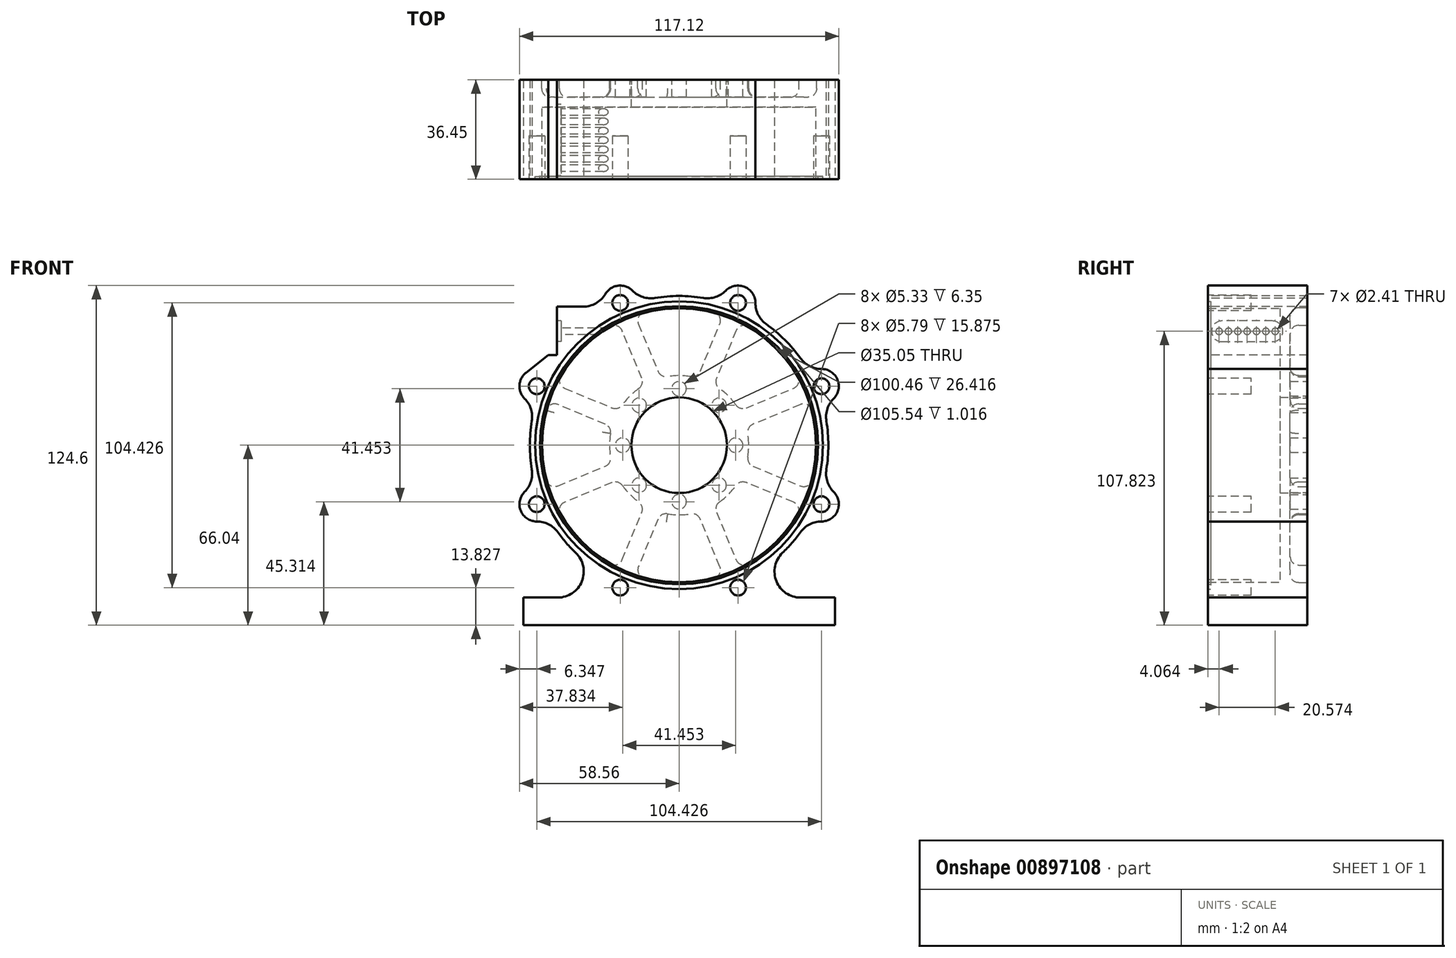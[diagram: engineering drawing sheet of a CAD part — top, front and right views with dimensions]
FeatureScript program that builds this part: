
annotation { "Feature Type Name" : "Feature", "Feature Type Description" : "" }
export const myFeature = defineFeature(function(context is Context, id is Id, definition is map)
    precondition{}
    {
        {
            var Q0;
            Q0=qCreatedBy(makeId("Front.planeOp"),FACE);
            var sketch = newSketch(context, id + "F0", { "sketchPlane" : qUnion([Q0])});
            skCircle(sketch, "E0", {"center": v(0, 0) * mm, "radius": 50.17 * mm, "construction": true});
            skArc(sketch, "E1", {"start": v(54.02, -8.84) * mm, "mid": v(54.74, 0) * mm, "end": v(54.02, 8.84) * mm});
            skCircle(sketch, "E2.cCircle", {"center": v(0, 0) * mm, "radius": 56.52 * mm, "construction": true});
            skLineSegment(sketch, "E2.0", {"start": v(52.21, -21.63) * mm, "end": v(21.63, -52.21) * mm, "construction": true});
            skLineSegment(sketch, "E2.1", {"start": v(21.63, -52.21) * mm, "end": v(-21.63, -52.21) * mm, "construction": true});
            skLineSegment(sketch, "E2.2", {"start": v(-21.63, -52.21) * mm, "end": v(-52.21, -21.63) * mm, "construction": true});
            skLineSegment(sketch, "E2.3", {"start": v(-52.21, -21.63) * mm, "end": v(-52.21, 21.63) * mm, "construction": true});
            skLineSegment(sketch, "E2.4", {"start": v(-52.21, 21.63) * mm, "end": v(-21.63, 52.21) * mm, "construction": true});
            skLineSegment(sketch, "E2.5", {"start": v(-21.63, 52.21) * mm, "end": v(21.63, 52.21) * mm, "construction": true});
            skLineSegment(sketch, "E2.6", {"start": v(21.63, 52.21) * mm, "end": v(52.21, 21.63) * mm, "construction": true});
            skLineSegment(sketch, "E2.7", {"start": v(52.21, 21.63) * mm, "end": v(52.21, -21.63) * mm, "construction": true});
            skArc(sketch, "E3", {"start": v(27.98, 52.2) * mm, "mid": v(24.06, 58.08) * mm, "end": v(17.13, 56.7) * mm});
            skArc(sketch, "E4", {"start": v(56.7, 17.13) * mm, "mid": v(58.08, 24.06) * mm, "end": v(52.2, 27.98) * mm});
            skArc(sketch, "E5", {"start": v(52.2, -27.98) * mm, "mid": v(58.08, -24.06) * mm, "end": v(56.7, -17.13) * mm});
            skArc(sketch, "E6", {"start": v(-56.7, -17.13) * mm, "mid": v(-58.08, -24.06) * mm, "end": v(-52.2, -27.98) * mm});
            skArc(sketch, "E7", {"start": v(-56.13, 26.62) * mm, "mid": v(-58.55, 22) * mm, "end": v(-56.7, 17.13) * mm});
            skArc(sketch, "E8.trimOffspring", {"start": v(44.45, 31.94) * mm, "mid": v(38.7, 38.7) * mm, "end": v(31.94, 44.45) * mm});
            skArc(sketch, "E9.trimOffspring", {"start": v(8.84, 54.02) * mm, "mid": v(0, 54.74) * mm, "end": v(-8.84, 54.02) * mm});
            skArc(sketch, "E10.trimOffspring", {"start": v(-54.02, 8.84) * mm, "mid": v(-54.74, 0) * mm, "end": v(-54.02, -8.84) * mm});
            skArc(sketch, "E11.trimOffspring", {"start": v(-44.45, -31.94) * mm, "mid": v(-41.35, -35.86) * mm, "end": v(-37.9, -39.48) * mm});
            skArc(sketch, "E12.trimOffspring", {"start": v(37.9, -39.48) * mm, "mid": v(41.35, -35.86) * mm, "end": v(44.45, -31.94) * mm});
            skLineSegment(sketch, "E13", {"start": v(-57.15, -55.88) * mm, "end": v(-57.15, -66.04) * mm});
            skLineSegment(sketch, "E14", {"start": v(-57.15, -66.04) * mm, "end": v(57.15, -66.04) * mm});
            skLineSegment(sketch, "E15", {"start": v(57.15, -66.04) * mm, "end": v(57.15, -55.88) * mm});
            skLineSegment(sketch, "E16", {"start": v(57.15, -55.88) * mm, "end": v(44.5, -55.88) * mm});
            skLineSegment(sketch, "E17", {"start": v(-57.15, -55.88) * mm, "end": v(-44.5, -55.88) * mm});
            skPoint(sketch, "E18", {"position": v(0, -66.04) * mm});
            skArc(sketch, "E19", {"start": v(-44.5, -55.88) * mm, "mid": v(-35.67, -49.91) * mm, "end": v(-37.9, -39.48) * mm});
            skArc(sketch, "E20", {"start": v(37.9, -39.48) * mm, "mid": v(35.67, -49.91) * mm, "end": v(44.5, -55.88) * mm});
            skPoint(sketch, "E21.visualSharp", {"position": v(-47.97, -26.36) * mm});
            skArc(sketch, "E21.filletArc", {"start": v(-44.45, -31.94) * mm, "mid": v(-47.85, -29.02) * mm, "end": v(-52.2, -27.98) * mm});
            skPoint(sketch, "E22.visualSharp", {"position": v(-52.56, -15.29) * mm});
            skArc(sketch, "E22.filletArc", {"start": v(-56.7, -17.13) * mm, "mid": v(-54.35, -13.3) * mm, "end": v(-54.02, -8.84) * mm});
            skPoint(sketch, "E23.visualSharp", {"position": v(-52.56, 15.29) * mm});
            skArc(sketch, "E23.filletArc", {"start": v(-54.02, 8.84) * mm, "mid": v(-54.35, 13.3) * mm, "end": v(-56.7, 17.13) * mm});
            skPoint(sketch, "E24.visualSharp", {"position": v(47.97, -26.36) * mm});
            skArc(sketch, "E24.filletArc", {"start": v(52.2, -27.98) * mm, "mid": v(47.85, -29.02) * mm, "end": v(44.45, -31.94) * mm});
            skPoint(sketch, "E25.visualSharp", {"position": v(52.56, -15.29) * mm});
            skArc(sketch, "E25.filletArc", {"start": v(54.02, -8.84) * mm, "mid": v(54.35, -13.3) * mm, "end": v(56.7, -17.13) * mm});
            skPoint(sketch, "E26.visualSharp", {"position": v(52.56, 15.29) * mm});
            skArc(sketch, "E26.filletArc", {"start": v(56.7, 17.13) * mm, "mid": v(54.35, 13.3) * mm, "end": v(54.02, 8.84) * mm});
            skPoint(sketch, "E27.visualSharp", {"position": v(47.97, 26.36) * mm});
            skArc(sketch, "E27.filletArc", {"start": v(44.45, 31.94) * mm, "mid": v(47.85, 29.02) * mm, "end": v(52.2, 27.98) * mm});
            skPoint(sketch, "E28.visualSharp", {"position": v(26.36, 47.97) * mm});
            skArc(sketch, "E28.filletArc", {"start": v(27.98, 52.2) * mm, "mid": v(29.02, 47.85) * mm, "end": v(31.94, 44.45) * mm});
            skPoint(sketch, "E29.visualSharp", {"position": v(15.29, 52.56) * mm});
            skArc(sketch, "E29.filletArc", {"start": v(8.84, 54.02) * mm, "mid": v(13.3, 54.35) * mm, "end": v(17.13, 56.7) * mm});
            skPoint(sketch, "E30.visualSharp", {"position": v(-15.29, 52.56) * mm});
            skLineSegment(sketch, "E31", {"start": v(-35.27, 50.8) * mm, "end": v(-44.8, 50.8) * mm});
            skLineSegment(sketch, "E32", {"start": v(-44.8, 50.8) * mm, "end": v(-44.8, 33.02) * mm});
            skArc(sketch, "E33", {"start": v(-17.13, 56.7) * mm, "mid": v(-22.41, 58.51) * mm, "end": v(-27.09, 55.46) * mm});
            skArc(sketch, "E34.filletArc", {"start": v(-17.13, 56.7) * mm, "mid": v(-13.3, 54.35) * mm, "end": v(-8.84, 54.02) * mm});
            skPoint(sketch, "E35.visualSharp", {"position": v(-27.82, 50.8) * mm});
            skArc(sketch, "E35.filletArc", {"start": v(-35.27, 50.8) * mm, "mid": v(-30.56, 52.05) * mm, "end": v(-27.09, 55.46) * mm});
            skLineSegment(sketch, "E36", {"start": v(-44.8, 33.02) * mm, "end": v(-47.97, 33.02) * mm});
            skLineSegment(sketch, "E37", {"start": v(-47.97, 33.02) * mm, "end": v(-56.13, 26.62) * mm});
            skSolve(sketch);
        }
        {
            var Q0;
            Q0=qSketchRegion(id+"F0",true);
            extrude(context, id + "F1", {"entities" : qUnion([Q0]), "oppositeDirection" : true, "depth" : 36.45 * mm});
        }
        {
            var Q0;
            Q0=qCreatedBy(makeId("Right.planeOp"),FACE);
            var sketch = newSketch(context, id + "F2", { "sketchPlane" : qUnion([Q0])});
            skLineSegment(sketch, "E38", {"start": v(0, 0) * mm, "end": v(0, 50.23) * mm});
            skLineSegment(sketch, "E39", {"start": v(26.42, 50.23) * mm, "end": v(0, 50.23) * mm});
            skLineSegment(sketch, "E40", {"start": v(26.42, 50.23) * mm, "end": v(26.42, 17.53) * mm});
            skLineSegment(sketch, "E41", {"start": v(36.45, 17.53) * mm, "end": v(26.42, 17.53) * mm});
            skLineSegment(sketch, "E42", {"start": v(36.45, 17.53) * mm, "end": v(36.45, 0) * mm});
            skLineSegment(sketch, "E43", {"start": v(0, 0) * mm, "end": v(36.45, 0) * mm});
            skLineSegment(sketch, "E44.bottom", {"start": v(1.02, 51) * mm, "end": v(0, 51) * mm});
            skLineSegment(sketch, "E44.top", {"start": v(1.02, 52.77) * mm, "end": v(0, 52.77) * mm});
            skLineSegment(sketch, "E44.left", {"start": v(0, 51) * mm, "end": v(0, 52.77) * mm});
            skLineSegment(sketch, "E44.right", {"start": v(1.02, 51) * mm, "end": v(1.02, 52.77) * mm});
            skSolve(sketch);
        }
        {
            var Q0;
            Q0=qSketchRegion(id+"F2",true);
            var Q1;
            Q1=sQuery(id+"F2.wireOp",EDGE,"E43");
            revolve(context, id + "F3", {"operationType" : NewBodyOperationType.REMOVE, "entities" : qUnion([Q0]), "axis" : qUnion([Q1]), "revolveType" : RevolveType.FULL, "oppositeDirection" : true});
        }
        {
            var Q0;
            Q0=makeQuery(id+"F1.opExtrude","SWEPT_FACE",FACE,{"disambiguationData":[OSD([sQuery(id+"F0.wireOp",EDGE,"E32")])]});
            var sketch = newSketch(context, id + "F4", { "sketchPlane" : qUnion([Q0])});
            skLineSegment(sketch, "E45", {"start": v(-23.62, 45.6) * mm, "end": v(-5.08, 45.6) * mm});
            skLineSegment(sketch, "E46", {"start": v(-5.08, 37.97) * mm, "end": v(-23.62, 37.97) * mm});
            skArc(sketch, "E47", {"start": v(-23.62, 45.6) * mm, "mid": v(-27.43, 41.78) * mm, "end": v(-23.62, 37.97) * mm});
            skArc(sketch, "E48", {"start": v(-5.08, 37.97) * mm, "mid": v(-1.27, 41.78) * mm, "end": v(-5.08, 45.6) * mm});
            skSolve(sketch);
        }
        {
            var Q0;
            Q0=qSketchRegion(id+"F4",true);
            extrude(context, id + "F5", {"entities" : qUnion([Q0]), "operationType" : NewBodyOperationType.REMOVE, "oppositeDirection" : true, "depth" : 1.52 * mm});
        }
        {
            var Q0;
            Q0=makeQuery(id+"F5.boolean.opBoolean","COPY",FACE,{"derivedFrom":makeQuery(id+"F5.opExtrude","CAP_FACE",FACE,{"disambiguationData":[OSD([sQuery(id+"F4.wireOp",EDGE,"E45"),sQuery(id+"F4.wireOp",EDGE,"E46"),sQuery(id+"F4.wireOp",EDGE,"E47"),sQuery(id+"F4.wireOp",EDGE,"E48")])],"isStart":false})});
            var sketch = newSketch(context, id + "F6", { "sketchPlane" : qUnion([Q0])});
            skCircle(sketch, "E49", {"center": v(-4.06, 41.78) * mm, "radius": 1.2 * mm});
            skPoint(sketch, "E50", {"position": v(-1.27, 41.78) * mm});
            skCircle(sketch, "E51.1.0.0", {"center": v(-7.5, 41.78) * mm, "radius": 1.2 * mm});
            skCircle(sketch, "E51.2.0.0", {"center": v(-10.92, 41.78) * mm, "radius": 1.2 * mm});
            skCircle(sketch, "E51.3.0.0", {"center": v(-14.35, 41.78) * mm, "radius": 1.2 * mm});
            skCircle(sketch, "E51.4.0.0", {"center": v(-17.78, 41.78) * mm, "radius": 1.2 * mm});
            skCircle(sketch, "E51.5.0.0", {"center": v(-21.2, 41.78) * mm, "radius": 1.2 * mm});
            skCircle(sketch, "E51.6.0.0", {"center": v(-24.64, 41.78) * mm, "radius": 1.2 * mm});
            skLineSegment(sketch, "E51.direction1", {"start": v(-4.06, 41.78) * mm, "end": v(-7.5, 41.78) * mm, "construction": true});
            skSolve(sketch);
        }
        {
            var Q0;
            Q0=qSketchRegion(id+"F6",true);
            extrude(context, id + "F7", {"entities" : qUnion([Q0]), "operationType" : NewBodyOperationType.REMOVE, "oppositeDirection" : true, "depth" : 25.4 * mm});
        }
        {
            var Q0;
            Q0=makeQuery(id+"F1.opExtrude","CAP_FACE",FACE,{"disambiguationData":[OSD([sQuery(id+"F0.wireOp",EDGE,"E1"),sQuery(id+"F0.wireOp",EDGE,"E3"),sQuery(id+"F0.wireOp",EDGE,"E4"),sQuery(id+"F0.wireOp",EDGE,"E5"),sQuery(id+"F0.wireOp",EDGE,"E6"),sQuery(id+"F0.wireOp",EDGE,"E7"),sQuery(id+"F0.wireOp",EDGE,"E8.trimOffspring"),sQuery(id+"F0.wireOp",EDGE,"E9.trimOffspring"),sQuery(id+"F0.wireOp",EDGE,"E10.trimOffspring"),sQuery(id+"F0.wireOp",EDGE,"E11.trimOffspring"),sQuery(id+"F0.wireOp",EDGE,"E12.trimOffspring"),sQuery(id+"F0.wireOp",EDGE,"E13"),sQuery(id+"F0.wireOp",EDGE,"E14"),sQuery(id+"F0.wireOp",EDGE,"E15"),sQuery(id+"F0.wireOp",EDGE,"E16"),sQuery(id+"F0.wireOp",EDGE,"E17"),sQuery(id+"F0.wireOp",EDGE,"E19"),sQuery(id+"F0.wireOp",EDGE,"E20"),sQuery(id+"F0.wireOp",EDGE,"E21.filletArc"),sQuery(id+"F0.wireOp",EDGE,"E22.filletArc"),sQuery(id+"F0.wireOp",EDGE,"E23.filletArc"),sQuery(id+"F0.wireOp",EDGE,"E24.filletArc"),sQuery(id+"F0.wireOp",EDGE,"E25.filletArc"),sQuery(id+"F0.wireOp",EDGE,"E26.filletArc"),sQuery(id+"F0.wireOp",EDGE,"E27.filletArc"),sQuery(id+"F0.wireOp",EDGE,"E28.filletArc"),sQuery(id+"F0.wireOp",EDGE,"E29.filletArc"),sQuery(id+"F0.wireOp",EDGE,"E31"),sQuery(id+"F0.wireOp",EDGE,"E32"),sQuery(id+"F0.wireOp",EDGE,"E33"),sQuery(id+"F0.wireOp",EDGE,"E34.filletArc"),sQuery(id+"F0.wireOp",EDGE,"E35.filletArc"),sQuery(id+"F0.wireOp",EDGE,"E36"),sQuery(id+"F0.wireOp",EDGE,"E37")])],"isStart":false});
            var sketch = newSketch(context, id + "F8", { "sketchPlane" : qUnion([Q0])});
            skPoint(sketch, "E52.center", {"position": v(0, 0) * mm});
            skArc(sketch, "E53", {"start": v(4.25, 25.17) * mm, "mid": v(0, 25.53) * mm, "end": v(-4.25, 25.17) * mm});
            skLineSegment(sketch, "E54", {"start": v(0, 0) * mm, "end": v(24.06, 58.08) * mm, "construction": true});
            skLineSegment(sketch, "E55", {"start": v(0, 0) * mm, "end": v(0, 17.53) * mm, "construction": true});
            skArc(sketch, "E56", {"start": v(12.8, 48.77) * mm, "mid": v(0, 50.42) * mm, "end": v(-12.8, 48.77) * mm});
            skLineSegment(sketch, "E57", {"start": v(14.92, 44.48) * mm, "end": v(7.71, 27.09) * mm});
            skLineSegment(sketch, "E58", {"start": v(-7.71, 27.09) * mm, "end": v(-14.92, 44.48) * mm});
            skPoint(sketch, "E59.visualSharp", {"position": v(-16.26, 47.72) * mm});
            skArc(sketch, "E59.filletArc", {"start": v(-12.8, 48.77) * mm, "mid": v(-14.83, 47.1) * mm, "end": v(-14.92, 44.48) * mm});
            skPoint(sketch, "E60.visualSharp", {"position": v(16.26, 47.72) * mm});
            skArc(sketch, "E60.filletArc", {"start": v(14.92, 44.48) * mm, "mid": v(14.83, 47.1) * mm, "end": v(12.8, 48.77) * mm});
            skPoint(sketch, "E61.visualSharp", {"position": v(6.7, 24.63) * mm});
            skArc(sketch, "E61.filletArc", {"start": v(4.25, 25.17) * mm, "mid": v(6.32, 25.52) * mm, "end": v(7.71, 27.09) * mm});
            skPoint(sketch, "E62.visualSharp", {"position": v(-6.7, 24.63) * mm});
            skArc(sketch, "E62.filletArc", {"start": v(-7.71, 27.09) * mm, "mid": v(-6.32, 25.52) * mm, "end": v(-4.25, 25.17) * mm});
            skArc(sketch, "E63.1.0", {"start": v(-43.53, 25.44) * mm, "mid": v(-43.8, 22.82) * mm, "end": v(-42, 20.9) * mm});
            skLineSegment(sketch, "E63.1.1", {"start": v(-24.6, 13.7) * mm, "end": v(-42, 20.9) * mm});
            skArc(sketch, "E63.1.2", {"start": v(-14.8, 20.8) * mm, "mid": v(-18.05, 18.05) * mm, "end": v(-20.8, 14.8) * mm});
            skArc(sketch, "E63.1.3", {"start": v(-24.6, 13.7) * mm, "mid": v(-22.51, 13.58) * mm, "end": v(-20.8, 14.8) * mm});
            skArc(sketch, "E63.1.4", {"start": v(-14.8, 20.8) * mm, "mid": v(-13.58, 22.51) * mm, "end": v(-13.7, 24.6) * mm});
            skLineSegment(sketch, "E63.1.5", {"start": v(-20.9, 42) * mm, "end": v(-13.7, 24.6) * mm});
            skArc(sketch, "E63.1.6", {"start": v(-20.9, 42) * mm, "mid": v(-22.82, 43.8) * mm, "end": v(-25.44, 43.53) * mm});
            skArc(sketch, "E63.1.7", {"start": v(-25.44, 43.53) * mm, "mid": v(-35.65, 35.65) * mm, "end": v(-43.53, 25.44) * mm});
            skArc(sketch, "E63.2.0", {"start": v(-48.77, -12.8) * mm, "mid": v(-47.1, -14.83) * mm, "end": v(-44.48, -14.92) * mm});
            skLineSegment(sketch, "E63.2.1", {"start": v(-27.09, -7.71) * mm, "end": v(-44.48, -14.92) * mm});
            skArc(sketch, "E63.2.2", {"start": v(-25.17, 4.25) * mm, "mid": v(-25.53, 0) * mm, "end": v(-25.17, -4.25) * mm});
            skArc(sketch, "E63.2.3", {"start": v(-27.09, -7.71) * mm, "mid": v(-25.52, -6.32) * mm, "end": v(-25.17, -4.25) * mm});
            skArc(sketch, "E63.2.4", {"start": v(-25.17, 4.25) * mm, "mid": v(-25.52, 6.32) * mm, "end": v(-27.09, 7.71) * mm});
            skLineSegment(sketch, "E63.2.5", {"start": v(-44.48, 14.92) * mm, "end": v(-27.09, 7.71) * mm});
            skArc(sketch, "E63.2.6", {"start": v(-44.48, 14.92) * mm, "mid": v(-47.1, 14.83) * mm, "end": v(-48.77, 12.8) * mm});
            skArc(sketch, "E63.2.7", {"start": v(-48.77, 12.8) * mm, "mid": v(-50.42, 0) * mm, "end": v(-48.77, -12.8) * mm});
            skArc(sketch, "E63.3.0", {"start": v(-25.44, -43.53) * mm, "mid": v(-22.82, -43.8) * mm, "end": v(-20.9, -42) * mm});
            skLineSegment(sketch, "E63.3.1", {"start": v(-13.7, -24.6) * mm, "end": v(-20.9, -42) * mm});
            skArc(sketch, "E63.3.2", {"start": v(-20.8, -14.8) * mm, "mid": v(-18.05, -18.05) * mm, "end": v(-14.8, -20.8) * mm});
            skArc(sketch, "E63.3.3", {"start": v(-13.7, -24.6) * mm, "mid": v(-13.58, -22.51) * mm, "end": v(-14.8, -20.8) * mm});
            skArc(sketch, "E63.3.4", {"start": v(-20.8, -14.8) * mm, "mid": v(-22.51, -13.58) * mm, "end": v(-24.6, -13.7) * mm});
            skLineSegment(sketch, "E63.3.5", {"start": v(-42, -20.9) * mm, "end": v(-24.6, -13.7) * mm});
            skArc(sketch, "E63.3.6", {"start": v(-42, -20.9) * mm, "mid": v(-43.8, -22.82) * mm, "end": v(-43.53, -25.44) * mm});
            skArc(sketch, "E63.3.7", {"start": v(-43.53, -25.44) * mm, "mid": v(-35.65, -35.65) * mm, "end": v(-25.44, -43.53) * mm});
            skArc(sketch, "E63.4.0", {"start": v(12.8, -48.77) * mm, "mid": v(14.83, -47.1) * mm, "end": v(14.92, -44.48) * mm});
            skLineSegment(sketch, "E63.4.1", {"start": v(7.71, -27.09) * mm, "end": v(14.92, -44.48) * mm});
            skArc(sketch, "E63.4.2", {"start": v(-4.25, -25.17) * mm, "mid": v(0, -25.53) * mm, "end": v(4.25, -25.17) * mm});
            skArc(sketch, "E63.4.3", {"start": v(7.71, -27.09) * mm, "mid": v(6.32, -25.52) * mm, "end": v(4.25, -25.17) * mm});
            skArc(sketch, "E63.4.4", {"start": v(-4.25, -25.17) * mm, "mid": v(-6.32, -25.52) * mm, "end": v(-7.71, -27.09) * mm});
            skLineSegment(sketch, "E63.4.5", {"start": v(-14.92, -44.48) * mm, "end": v(-7.71, -27.09) * mm});
            skArc(sketch, "E63.4.6", {"start": v(-14.92, -44.48) * mm, "mid": v(-14.83, -47.1) * mm, "end": v(-12.8, -48.77) * mm});
            skArc(sketch, "E63.4.7", {"start": v(-12.8, -48.77) * mm, "mid": v(0, -50.42) * mm, "end": v(12.8, -48.77) * mm});
            skArc(sketch, "E63.5.0", {"start": v(43.53, -25.44) * mm, "mid": v(43.8, -22.82) * mm, "end": v(42, -20.9) * mm});
            skLineSegment(sketch, "E63.5.1", {"start": v(24.6, -13.7) * mm, "end": v(42, -20.9) * mm});
            skArc(sketch, "E63.5.2", {"start": v(14.8, -20.8) * mm, "mid": v(18.05, -18.05) * mm, "end": v(20.8, -14.8) * mm});
            skArc(sketch, "E63.5.3", {"start": v(24.6, -13.7) * mm, "mid": v(22.51, -13.58) * mm, "end": v(20.8, -14.8) * mm});
            skArc(sketch, "E63.5.4", {"start": v(14.8, -20.8) * mm, "mid": v(13.58, -22.51) * mm, "end": v(13.7, -24.6) * mm});
            skLineSegment(sketch, "E63.5.5", {"start": v(20.9, -42) * mm, "end": v(13.7, -24.6) * mm});
            skArc(sketch, "E63.5.6", {"start": v(20.9, -42) * mm, "mid": v(22.82, -43.8) * mm, "end": v(25.44, -43.53) * mm});
            skArc(sketch, "E63.5.7", {"start": v(25.44, -43.53) * mm, "mid": v(35.65, -35.65) * mm, "end": v(43.53, -25.44) * mm});
            skArc(sketch, "E63.6.0", {"start": v(48.77, 12.8) * mm, "mid": v(47.1, 14.83) * mm, "end": v(44.48, 14.92) * mm});
            skLineSegment(sketch, "E63.6.1", {"start": v(27.09, 7.71) * mm, "end": v(44.48, 14.92) * mm});
            skArc(sketch, "E63.6.2", {"start": v(25.17, -4.25) * mm, "mid": v(25.53, 0) * mm, "end": v(25.17, 4.25) * mm});
            skArc(sketch, "E63.6.3", {"start": v(27.09, 7.71) * mm, "mid": v(25.52, 6.32) * mm, "end": v(25.17, 4.25) * mm});
            skArc(sketch, "E63.6.4", {"start": v(25.17, -4.25) * mm, "mid": v(25.52, -6.32) * mm, "end": v(27.09, -7.71) * mm});
            skLineSegment(sketch, "E63.6.5", {"start": v(44.48, -14.92) * mm, "end": v(27.09, -7.71) * mm});
            skArc(sketch, "E63.6.6", {"start": v(44.48, -14.92) * mm, "mid": v(47.1, -14.83) * mm, "end": v(48.77, -12.8) * mm});
            skArc(sketch, "E63.6.7", {"start": v(48.77, -12.8) * mm, "mid": v(50.42, 0) * mm, "end": v(48.77, 12.8) * mm});
            skArc(sketch, "E63.7.0", {"start": v(25.44, 43.53) * mm, "mid": v(22.82, 43.8) * mm, "end": v(20.9, 42) * mm});
            skLineSegment(sketch, "E63.7.1", {"start": v(13.7, 24.6) * mm, "end": v(20.9, 42) * mm});
            skArc(sketch, "E63.7.2", {"start": v(20.8, 14.8) * mm, "mid": v(18.05, 18.05) * mm, "end": v(14.8, 20.8) * mm});
            skArc(sketch, "E63.7.3", {"start": v(13.7, 24.6) * mm, "mid": v(13.58, 22.51) * mm, "end": v(14.8, 20.8) * mm});
            skArc(sketch, "E63.7.4", {"start": v(20.8, 14.8) * mm, "mid": v(22.51, 13.58) * mm, "end": v(24.6, 13.7) * mm});
            skLineSegment(sketch, "E63.7.5", {"start": v(42, 20.9) * mm, "end": v(24.6, 13.7) * mm});
            skArc(sketch, "E63.7.6", {"start": v(42, 20.9) * mm, "mid": v(43.8, 22.82) * mm, "end": v(43.53, 25.44) * mm});
            skArc(sketch, "E63.7.7", {"start": v(43.53, 25.44) * mm, "mid": v(35.65, 35.65) * mm, "end": v(25.44, 43.53) * mm});
            skSolve(sketch);
        }
        {
            var Q0;
            Q0=qSketchRegion(id+"F8",true);
            extrude(context, id + "F9", {"entities" : qUnion([Q0]), "operationType" : NewBodyOperationType.REMOVE, "oppositeDirection" : true, "depth" : 6.35 * mm});
        }
        {
            var Q0;
            Q0=makeQuery(id+"F9.boolean.opBoolean","COPY",FACE,{"derivedFrom":makeQuery(id+"F9.opExtrude","CAP_FACE",FACE,{"disambiguationData":[OSD([sQuery(id+"F8.wireOp",EDGE,"E53"),sQuery(id+"F8.wireOp",EDGE,"E56"),sQuery(id+"F8.wireOp",EDGE,"E57"),sQuery(id+"F8.wireOp",EDGE,"E58"),sQuery(id+"F8.wireOp",EDGE,"E59.filletArc"),sQuery(id+"F8.wireOp",EDGE,"E60.filletArc"),sQuery(id+"F8.wireOp",EDGE,"E61.filletArc"),sQuery(id+"F8.wireOp",EDGE,"E62.filletArc")])],"isStart":false})});
            var Q1;
            Q1=makeQuery(id+"F9.boolean.opBoolean","COPY",FACE,{"derivedFrom":makeQuery(id+"F9.opExtrude","CAP_FACE",FACE,{"disambiguationData":[OSD([sQuery(id+"F8.wireOp",EDGE,"E63.7.0"),sQuery(id+"F8.wireOp",EDGE,"E63.7.1"),sQuery(id+"F8.wireOp",EDGE,"E63.7.2"),sQuery(id+"F8.wireOp",EDGE,"E63.7.3"),sQuery(id+"F8.wireOp",EDGE,"E63.7.4"),sQuery(id+"F8.wireOp",EDGE,"E63.7.5"),sQuery(id+"F8.wireOp",EDGE,"E63.7.6"),sQuery(id+"F8.wireOp",EDGE,"E63.7.7")])],"isStart":false})});
            var Q2;
            Q2=makeQuery(id+"F9.boolean.opBoolean","COPY",FACE,{"derivedFrom":makeQuery(id+"F9.opExtrude","CAP_FACE",FACE,{"disambiguationData":[OSD([sQuery(id+"F8.wireOp",EDGE,"E63.6.0"),sQuery(id+"F8.wireOp",EDGE,"E63.6.1"),sQuery(id+"F8.wireOp",EDGE,"E63.6.2"),sQuery(id+"F8.wireOp",EDGE,"E63.6.3"),sQuery(id+"F8.wireOp",EDGE,"E63.6.4"),sQuery(id+"F8.wireOp",EDGE,"E63.6.5"),sQuery(id+"F8.wireOp",EDGE,"E63.6.6"),sQuery(id+"F8.wireOp",EDGE,"E63.6.7")])],"isStart":false})});
            var Q3;
            Q3=makeQuery(id+"F9.boolean.opBoolean","COPY",FACE,{"derivedFrom":makeQuery(id+"F9.opExtrude","CAP_FACE",FACE,{"disambiguationData":[OSD([sQuery(id+"F8.wireOp",EDGE,"E63.5.0"),sQuery(id+"F8.wireOp",EDGE,"E63.5.1"),sQuery(id+"F8.wireOp",EDGE,"E63.5.2"),sQuery(id+"F8.wireOp",EDGE,"E63.5.3"),sQuery(id+"F8.wireOp",EDGE,"E63.5.4"),sQuery(id+"F8.wireOp",EDGE,"E63.5.5"),sQuery(id+"F8.wireOp",EDGE,"E63.5.6"),sQuery(id+"F8.wireOp",EDGE,"E63.5.7")])],"isStart":false})});
            var Q4;
            Q4=makeQuery(id+"F9.boolean.opBoolean","COPY",FACE,{"derivedFrom":makeQuery(id+"F9.opExtrude","CAP_FACE",FACE,{"disambiguationData":[OSD([sQuery(id+"F8.wireOp",EDGE,"E63.4.0"),sQuery(id+"F8.wireOp",EDGE,"E63.4.1"),sQuery(id+"F8.wireOp",EDGE,"E63.4.2"),sQuery(id+"F8.wireOp",EDGE,"E63.4.3"),sQuery(id+"F8.wireOp",EDGE,"E63.4.4"),sQuery(id+"F8.wireOp",EDGE,"E63.4.5"),sQuery(id+"F8.wireOp",EDGE,"E63.4.6"),sQuery(id+"F8.wireOp",EDGE,"E63.4.7")])],"isStart":false})});
            var Q5;
            Q5=makeQuery(id+"F9.boolean.opBoolean","COPY",FACE,{"derivedFrom":makeQuery(id+"F9.opExtrude","CAP_FACE",FACE,{"disambiguationData":[OSD([sQuery(id+"F8.wireOp",EDGE,"E63.3.0"),sQuery(id+"F8.wireOp",EDGE,"E63.3.1"),sQuery(id+"F8.wireOp",EDGE,"E63.3.2"),sQuery(id+"F8.wireOp",EDGE,"E63.3.3"),sQuery(id+"F8.wireOp",EDGE,"E63.3.4"),sQuery(id+"F8.wireOp",EDGE,"E63.3.5"),sQuery(id+"F8.wireOp",EDGE,"E63.3.6"),sQuery(id+"F8.wireOp",EDGE,"E63.3.7")])],"isStart":false})});
            var Q6;
            Q6=makeQuery(id+"F9.boolean.opBoolean","COPY",FACE,{"derivedFrom":makeQuery(id+"F9.opExtrude","CAP_FACE",FACE,{"disambiguationData":[OSD([sQuery(id+"F8.wireOp",EDGE,"E63.2.0"),sQuery(id+"F8.wireOp",EDGE,"E63.2.1"),sQuery(id+"F8.wireOp",EDGE,"E63.2.2"),sQuery(id+"F8.wireOp",EDGE,"E63.2.3"),sQuery(id+"F8.wireOp",EDGE,"E63.2.4"),sQuery(id+"F8.wireOp",EDGE,"E63.2.5"),sQuery(id+"F8.wireOp",EDGE,"E63.2.6"),sQuery(id+"F8.wireOp",EDGE,"E63.2.7")])],"isStart":false})});
            var Q7;
            Q7=makeQuery(id+"F9.boolean.opBoolean","COPY",FACE,{"derivedFrom":makeQuery(id+"F9.opExtrude","CAP_FACE",FACE,{"disambiguationData":[OSD([sQuery(id+"F8.wireOp",EDGE,"E63.1.0"),sQuery(id+"F8.wireOp",EDGE,"E63.1.1"),sQuery(id+"F8.wireOp",EDGE,"E63.1.2"),sQuery(id+"F8.wireOp",EDGE,"E63.1.3"),sQuery(id+"F8.wireOp",EDGE,"E63.1.4"),sQuery(id+"F8.wireOp",EDGE,"E63.1.5"),sQuery(id+"F8.wireOp",EDGE,"E63.1.6"),sQuery(id+"F8.wireOp",EDGE,"E63.1.7")])],"isStart":false})});
            fillet(context, id + "F10", {"entities" : qUnion([Q0, Q1, Q2, Q3, Q4, Q5, Q6, Q7]), "radius" : 3.17 * mm, "tangentPropagation" : true, "allowEdgeOverflow" : false});
        }
        {
            var Q0;
            Q0=makeQuery(id+"F1.opExtrude","CAP_FACE",FACE,{"disambiguationData":[OSD([sQuery(id+"F0.wireOp",EDGE,"E1"),sQuery(id+"F0.wireOp",EDGE,"E3"),sQuery(id+"F0.wireOp",EDGE,"E4"),sQuery(id+"F0.wireOp",EDGE,"E5"),sQuery(id+"F0.wireOp",EDGE,"E6"),sQuery(id+"F0.wireOp",EDGE,"E7"),sQuery(id+"F0.wireOp",EDGE,"E8.trimOffspring"),sQuery(id+"F0.wireOp",EDGE,"E9.trimOffspring"),sQuery(id+"F0.wireOp",EDGE,"E10.trimOffspring"),sQuery(id+"F0.wireOp",EDGE,"E11.trimOffspring"),sQuery(id+"F0.wireOp",EDGE,"E12.trimOffspring"),sQuery(id+"F0.wireOp",EDGE,"E13"),sQuery(id+"F0.wireOp",EDGE,"E14"),sQuery(id+"F0.wireOp",EDGE,"E15"),sQuery(id+"F0.wireOp",EDGE,"E16"),sQuery(id+"F0.wireOp",EDGE,"E17"),sQuery(id+"F0.wireOp",EDGE,"E19"),sQuery(id+"F0.wireOp",EDGE,"E20"),sQuery(id+"F0.wireOp",EDGE,"E21.filletArc"),sQuery(id+"F0.wireOp",EDGE,"E22.filletArc"),sQuery(id+"F0.wireOp",EDGE,"E23.filletArc"),sQuery(id+"F0.wireOp",EDGE,"E24.filletArc"),sQuery(id+"F0.wireOp",EDGE,"E25.filletArc"),sQuery(id+"F0.wireOp",EDGE,"E26.filletArc"),sQuery(id+"F0.wireOp",EDGE,"E27.filletArc"),sQuery(id+"F0.wireOp",EDGE,"E28.filletArc"),sQuery(id+"F0.wireOp",EDGE,"E29.filletArc"),sQuery(id+"F0.wireOp",EDGE,"E31"),sQuery(id+"F0.wireOp",EDGE,"E32"),sQuery(id+"F0.wireOp",EDGE,"E33"),sQuery(id+"F0.wireOp",EDGE,"E34.filletArc"),sQuery(id+"F0.wireOp",EDGE,"E35.filletArc"),sQuery(id+"F0.wireOp",EDGE,"E36"),sQuery(id+"F0.wireOp",EDGE,"E37")])],"isStart":false});
            var sketch = newSketch(context, id + "F11", { "sketchPlane" : qUnion([Q0])});
            skCircle(sketch, "E64", {"center": v(0, 20.73) * mm, "radius": 2.67 * mm});
            skCircle(sketch, "E65.1.0", {"center": v(-14.66, 14.66) * mm, "radius": 2.67 * mm});
            skCircle(sketch, "E65.2.0", {"center": v(-20.73, 0) * mm, "radius": 2.67 * mm});
            skCircle(sketch, "E65.3.0", {"center": v(-14.66, -14.66) * mm, "radius": 2.67 * mm});
            skCircle(sketch, "E65.4.0", {"center": v(0, -20.73) * mm, "radius": 2.67 * mm});
            skCircle(sketch, "E65.5.0", {"center": v(14.66, -14.66) * mm, "radius": 2.67 * mm});
            skCircle(sketch, "E65.6.0", {"center": v(20.73, 0) * mm, "radius": 2.67 * mm});
            skCircle(sketch, "E65.7.0", {"center": v(14.66, 14.66) * mm, "radius": 2.67 * mm});
            skPoint(sketch, "E65.center", {"position": v(0, 0) * mm});
            skSolve(sketch);
        }
        {
            var Q0;
            Q0=qSketchRegion(id+"F11",true);
            extrude(context, id + "F12", {"entities" : qUnion([Q0]), "operationType" : NewBodyOperationType.REMOVE, "oppositeDirection" : true, "depth" : 6.35 * mm});
        }
        {
            var Q0;
            Q0=qCreatedBy(makeId("Front.planeOp"),FACE);
            var sketch = newSketch(context, id + "F13", { "sketchPlane" : qUnion([Q0])});
            skCircle(sketch, "E66", {"center": v(21.63, 52.21) * mm, "radius": 2.9 * mm});
            skCircle(sketch, "E67.1.0", {"center": v(-21.63, 52.21) * mm, "radius": 2.9 * mm});
            skCircle(sketch, "E67.2.0", {"center": v(-52.21, 21.63) * mm, "radius": 2.9 * mm});
            skCircle(sketch, "E67.3.0", {"center": v(-52.21, -21.63) * mm, "radius": 2.9 * mm});
            skCircle(sketch, "E67.4.0", {"center": v(-21.63, -52.21) * mm, "radius": 2.9 * mm});
            skCircle(sketch, "E67.5.0", {"center": v(21.63, -52.21) * mm, "radius": 2.9 * mm});
            skCircle(sketch, "E67.6.0", {"center": v(52.21, -21.63) * mm, "radius": 2.9 * mm});
            skCircle(sketch, "E67.7.0", {"center": v(52.21, 21.63) * mm, "radius": 2.9 * mm});
            skPoint(sketch, "E67.center", {"position": v(0, 0) * mm});
            skSolve(sketch);
        }
        {
            var Q0;
            Q0=qSketchRegion(id+"F13",true);
            extrude(context, id + "F14", {"entities" : qUnion([Q0]), "operationType" : NewBodyOperationType.REMOVE, "oppositeDirection" : true, "depth" : 15.88 * mm});
        }
    });
